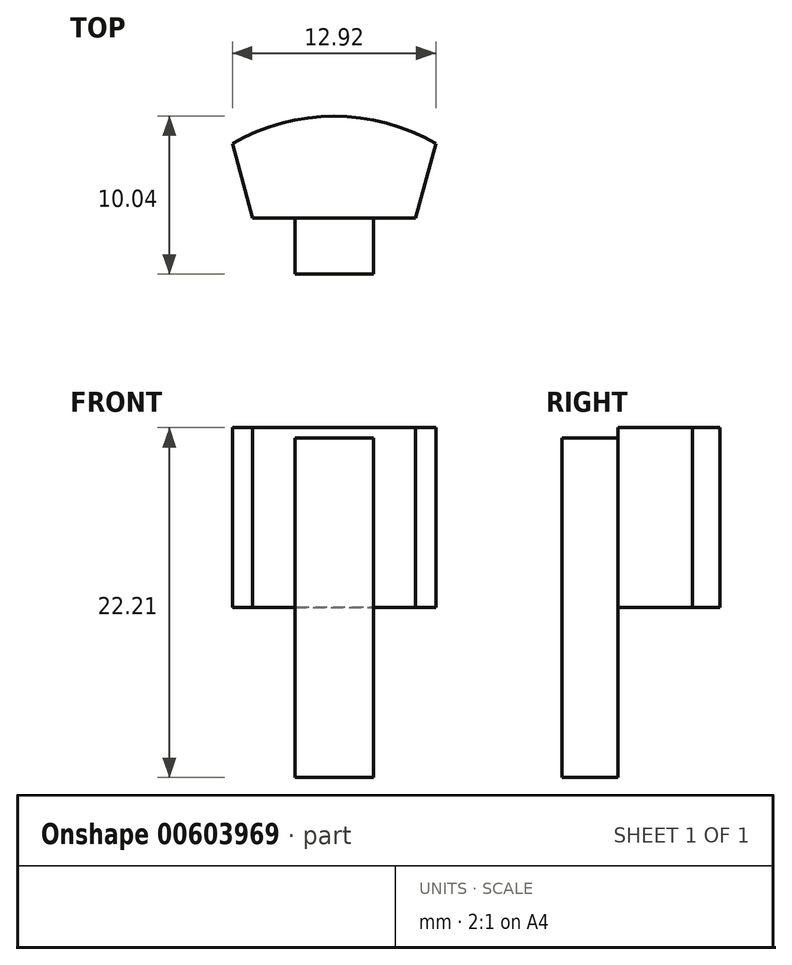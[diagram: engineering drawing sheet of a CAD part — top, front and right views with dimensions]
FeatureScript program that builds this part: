
annotation { "Feature Type Name" : "Feature", "Feature Type Description" : "" }
export const myFeature = defineFeature(function(context is Context, id is Id, definition is map)
    precondition{}
    {
        {
            var Q0;
            Q0=qCreatedBy(makeId("Front.planeOp"),FACE);
            var sketch = newSketch(context, id + "F0", { "sketchPlane" : qUnion([Q0])});
            skLineSegment(sketch, "E0.bottom", {"start": v(2.49, -10.78) * mm, "end": v(-2.49, -10.78) * mm});
            skLineSegment(sketch, "E0.top", {"start": v(2.49, 10.78) * mm, "end": v(-2.49, 10.78) * mm});
            skLineSegment(sketch, "E0.left", {"start": v(2.49, -10.78) * mm, "end": v(2.49, 10.78) * mm});
            skLineSegment(sketch, "E0.right", {"start": v(-2.49, -10.78) * mm, "end": v(-2.49, 10.78) * mm});
            skPoint(sketch, "E0.middle", {"position": v(0, 0) * mm});
            skSolve(sketch);
        }
        {
            var Q0;
            Q0=qCreatedBy(makeId("Top.planeOp"),FACE);
            var sketch = newSketch(context, id + "F1", { "sketchPlane" : qUnion([Q0])});
            skLineSegment(sketch, "E1", {"start": v(-11.15, 0) * mm, "end": v(11.15, 0) * mm});
            skArc(sketch, "E2", {"start": v(11.15, 0) * mm, "mid": v(0, 6.48) * mm, "end": v(-11.15, 0) * mm});
            skSolve(sketch);
        }
        {
            var Q0;
            Q0=makeQuery(id+"F1.imprint","IMPRINT",FACE,{"disambiguationData":[TD([[makeQuery(id+"F1.imprint","IMPRINT",EDGE,{"derivedFrom":sQuery(id+"F1.wireOp",EDGE,"E1")}),1.0]])]});
            extrude(context, id + "F2", {"entities" : qUnion([Q0]), "depth" : 11.43 * mm, "offsetDistance" : 25.4 * mm});
        }
        {
            var Q0;
            Q0=makeQuery(id+"F0.imprint","IMPRINT",FACE,{"disambiguationData":[TD([[makeQuery(id+"F0.imprint","IMPRINT",EDGE,{"derivedFrom":sQuery(id+"F0.wireOp",EDGE,"E0.bottom")}),-1.0]])]});
            extrude(context, id + "F3", {"entities" : qUnion([Q0]), "operationType" : NewBodyOperationType.ADD, "depth" : 3.56 * mm, "offsetDistance" : 25.4 * mm});
        }
        {
            var Q0;
            {var subQ0=sQuery(id+"F1.wireOp",EDGE,"E2");var subQ1=sQuery(id+"F1.wireOp",EDGE,"E1");Q0=makeQuery(id+"F2.opExtrude","SWEPT_EDGE",EDGE,{"disambiguationData":[OSD([subQ1,subQ0]),TDD([makeQuery(id+"F1.imprint","INTERSECT",VERTEX,{"disambiguationData":[OD(0.0)],"derivedFrom":[subQ1,subQ0]})])]});}
            var Q1;
            {var subQ0=sQuery(id+"F1.wireOp",EDGE,"E2");var subQ1=sQuery(id+"F1.wireOp",EDGE,"E1");Q1=makeQuery(id+"F2.opExtrude","SWEPT_EDGE",EDGE,{"disambiguationData":[OSD([subQ1,subQ0]),TDD([makeQuery(id+"F1.imprint","INTERSECT",VERTEX,{"disambiguationData":[OD(1.0)],"derivedFrom":[subQ1,subQ0]})])]});}
            chamfer(context, id + "F4", {"entities" : qUnion([Q0, Q1]), "width" : 2.54 * mm, "tangentPropagation" : true});
        }
    });
